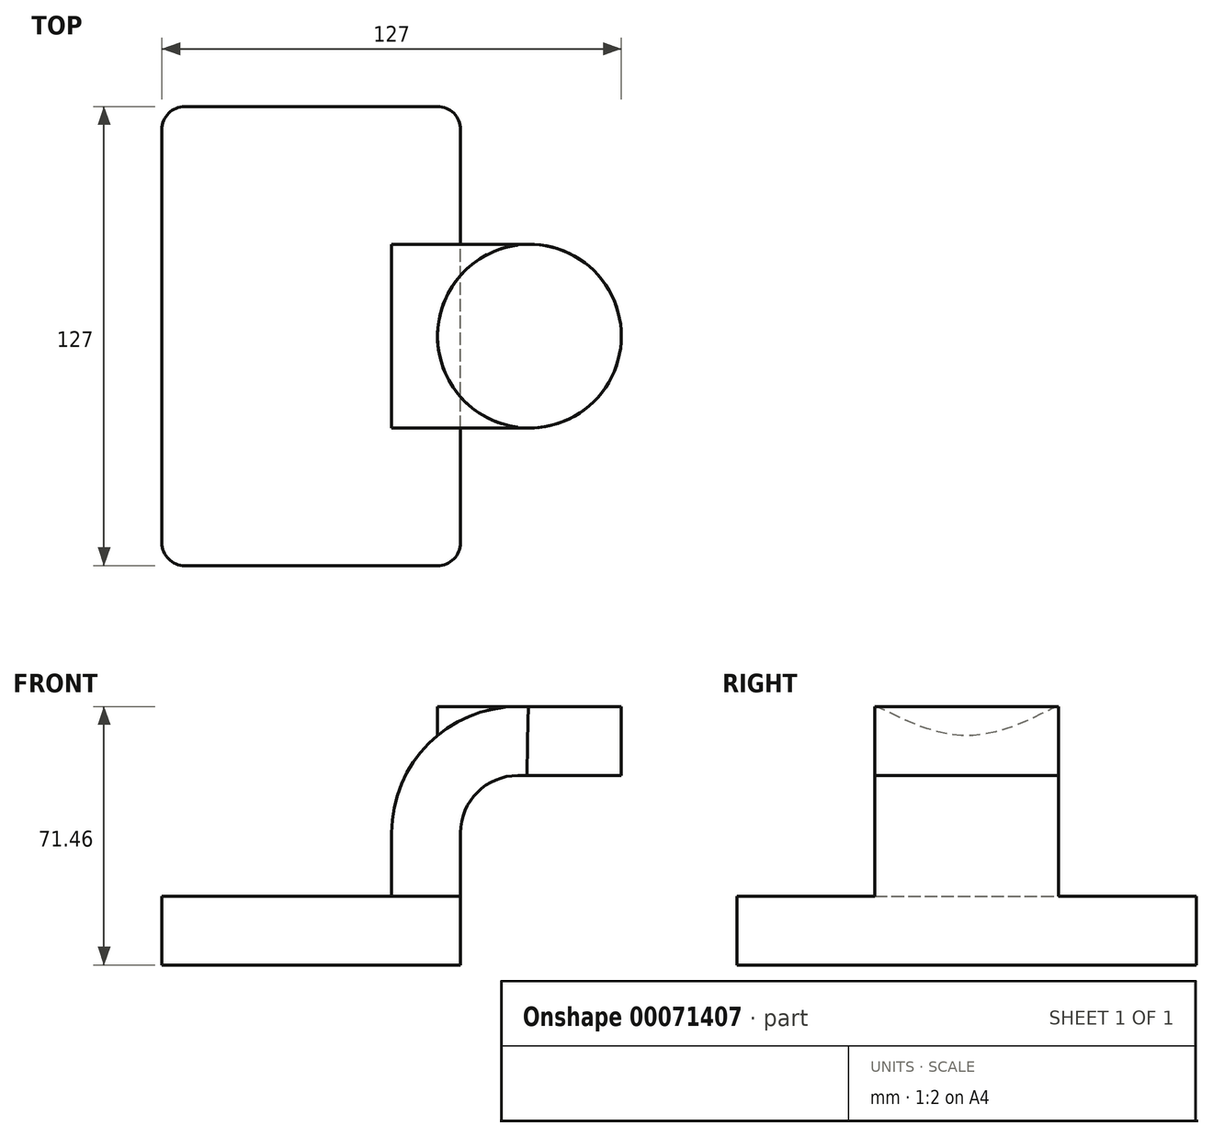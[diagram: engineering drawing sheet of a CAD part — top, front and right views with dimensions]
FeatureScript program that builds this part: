
annotation { "Feature Type Name" : "Feature", "Feature Type Description" : "" }
export const myFeature = defineFeature(function(context is Context, id is Id, definition is map)
    precondition{}
    {
        {
            var Q0;
            Q0=qCreatedBy(makeId("Front.planeOp"),FACE);
            var sketch = newSketch(context, id + "F0", { "sketchPlane" : qUnion([Q0])});
            skLineSegment(sketch, "E0.rect.bottom", {"start": v(41.27, 9.53) * mm, "end": v(-41.28, 9.53) * mm});
            skLineSegment(sketch, "E0.rect.top", {"start": v(41.28, -9.52) * mm, "end": v(-41.27, -9.52) * mm});
            skLineSegment(sketch, "E0.rect.left", {"start": v(41.28, 9.53) * mm, "end": v(41.28, -9.52) * mm});
            skLineSegment(sketch, "E0.rect.right", {"start": v(-41.28, 9.53) * mm, "end": v(-41.27, -9.52) * mm});
            skPoint(sketch, "E0.rect.middle", {"position": v(0, 0) * mm});
            skLineSegment(sketch, "E1", {"start": v(41.27, 9.53) * mm, "end": v(41.27, 27) * mm});
            skLineSegment(sketch, "E2.rect.bottom", {"start": v(111.12, 38.1) * mm, "end": v(60.33, 38.1) * mm});
            skLineSegment(sketch, "E2.rect.top", {"start": v(111.12, 66.68) * mm, "end": v(60.33, 66.68) * mm});
            skLineSegment(sketch, "E2.rect.left", {"start": v(111.13, 38.1) * mm, "end": v(111.13, 66.68) * mm});
            skLineSegment(sketch, "E2.rect.right", {"start": v(60.33, 38.1) * mm, "end": v(60.33, 66.68) * mm});
            skPoint(sketch, "E2.rect.middle", {"position": v(85.73, 52.39) * mm});
            skArc(sketch, "E3", {"start": v(41.28, 27) * mm, "mid": v(45.92, 38.23) * mm, "end": v(57.15, 42.88) * mm});
            skLineSegment(sketch, "E4", {"start": v(57.15, 42.88) * mm, "end": v(85.74, 42.88) * mm});
            skLineSegment(sketch, "E5.0", {"start": v(57.15, 61.93) * mm, "end": v(85.74, 61.93) * mm});
            skArc(sketch, "E5.1", {"start": v(22.23, 27) * mm, "mid": v(32.45, 51.7) * mm, "end": v(57.15, 61.93) * mm});
            skLineSegment(sketch, "E5.2", {"start": v(22.23, 9.53) * mm, "end": v(22.23, 27) * mm});
            skLineSegment(sketch, "E6", {"start": v(85.72, 66.68) * mm, "end": v(85.74, 38.1) * mm});
            skFitSpline(sketch, "E7", {"points": [v(57.15, 61.93) * mm, v(-41.28, 9.53) * mm], "startDerivative": vector(-159.22, 0.06) * mm, "endDerivative": vector(-55.21, -73.28) * mm});
            skSolve(sketch);
        }
        {
            var Q0;
            Q0=makeQuery(id+"F0.imprint","IMPRINT",FACE,{"disambiguationData":[TD([[makeQuery(id+"F0.imprint","IMPRINT",EDGE,{"derivedFrom":sQuery(id+"F0.wireOp",EDGE,"E0.rect.top")}),-1.0]])]});
            extrude(context, id + "F1", {"entities" : qUnion([Q0]), "depth" : 127 * mm, "symmetric" : true});
        }
        {
            var Q0;
            {var subQ6=sQuery(id+"F0.wireOp",EDGE,"E1");Q0=makeQuery(id+"F0.imprint","IMPRINT",FACE,{"disambiguationData":[TD([[makeQuery(id+"F0.imprint","IMPRINT",EDGE,{"derivedFrom":subQ6}),1.0]])]});}
            extrude(context, id + "F2", {"entities" : qUnion([Q0]), "operationType" : NewBodyOperationType.ADD, "depth" : 50.8 * mm, "symmetric" : true});
        }
        {
            var Q0;
            Q0=makeQuery(id+"F0.imprint","IMPRINT",FACE,{"disambiguationData":[TD([[makeQuery(id+"F0.imprint","IMPRINT",EDGE,{"derivedFrom":sQuery(id+"F0.wireOp",EDGE,"E5.1")}),1.0]])]});
            extrude(context, id + "F3", {"entities" : qUnion([Q0]), "operationType" : NewBodyOperationType.ADD, "depth" : 15.88 * mm, "symmetric" : true});
        }
        {
            var Q0;
            {var subQ0=sQuery(id+"F0.wireOp",EDGE,"E4");var subQ1=sQuery(id+"F0.wireOp",EDGE,"E2.rect.right");var subQ2=makeQuery(id+"F0.imprint","INTERSECT",VERTEX,{"derivedFrom":[subQ1,subQ0]});Q0=makeQuery(id+"F0.imprint","IMPRINT",FACE,{"disambiguationData":[TD([[makeQuery(id+"F0.imprint","IMPRINT",EDGE,{"disambiguationData":[TD([[subQ2,-1.0]])],"derivedFrom":subQ1}),-1.0]])]});}
            var Q1;
            Q1=sQuery(id+"F0.wireOp",EDGE,"E2.rect.right");
            revolve(context, id + "F4", {"operationType" : NewBodyOperationType.ADD, "entities" : qUnion([Q0]), "axis" : qUnion([Q1]), "revolveType" : RevolveType.FULL});
        }
        {
            var Q0;
            Q0=makeQuery(id+"F1.opExtrude","CAP_EDGE",EDGE,{"disambiguationData":[OSD([sQuery(id+"F0.wireOp",EDGE,"E0.rect.left")])],"isStart":false});
            var Q1;
            Q1=makeQuery(id+"F1.opExtrude","CAP_EDGE",EDGE,{"disambiguationData":[OSD([sQuery(id+"F0.wireOp",EDGE,"E0.rect.right")])],"isStart":false});
            var Q2;
            Q2=makeQuery(id+"F1.opExtrude","CAP_EDGE",EDGE,{"disambiguationData":[OSD([sQuery(id+"F0.wireOp",EDGE,"E0.rect.right")])],"isStart":true});
            var Q3;
            Q3=makeQuery(id+"F1.opExtrude","CAP_EDGE",EDGE,{"disambiguationData":[OSD([sQuery(id+"F0.wireOp",EDGE,"E0.rect.left")])],"isStart":true});
            fillet(context, id + "F5", {"entities" : qUnion([Q0, Q1, Q2, Q3]), "radius" : 6.35 * mm, "tangentPropagation" : true, "allowEdgeOverflow" : false});
        }
    });
